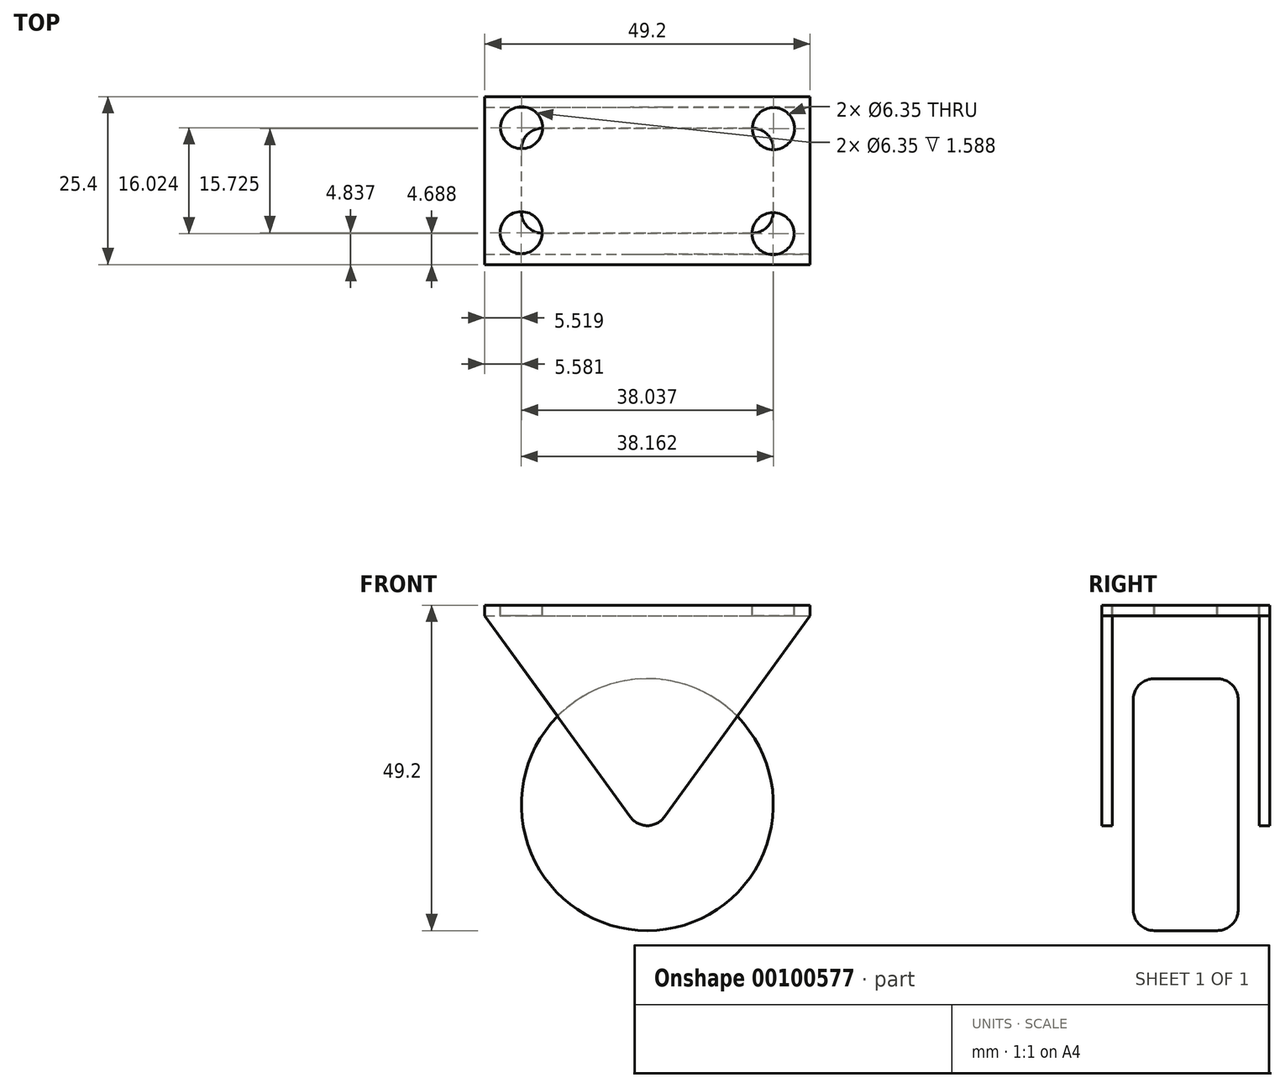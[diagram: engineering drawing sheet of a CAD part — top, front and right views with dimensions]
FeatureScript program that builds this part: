
annotation { "Feature Type Name" : "Feature", "Feature Type Description" : "" }
export const myFeature = defineFeature(function(context is Context, id is Id, definition is map)
    precondition{}
    {
        {
            var Q0;
            Q0=qCreatedBy(makeId("Front.planeOp"),FACE);
            var sketch = newSketch(context, id + "F0", { "sketchPlane" : qUnion([Q0])});
            skCircle(sketch, "E0", {"center": v(0, 0) * mm, "radius": 19.05 * mm});
            skSolve(sketch);
        }
        {
            var Q0;
            Q0=makeQuery(id+"F0.imprint","IMPRINT",FACE,{"disambiguationData":[TD([[makeQuery(id+"F0.imprint","IMPRINT",EDGE,{"derivedFrom":sQuery(id+"F0.wireOp",EDGE,"E0")}),1.0]])]});
            extrude(context, id + "F1", {"entities" : qUnion([Q0]), "endBound" : BoundingType.SYMMETRIC, "depth" : 15.88 * mm});
        }
        {
            var Q0;
            Q0=makeQuery(id+"F1.opExtrude","CAP_EDGE",EDGE,{"disambiguationData":[OSD([sQuery(id+"F0.wireOp",EDGE,"E0")])],"isStart":true});
            var Q1;
            Q1=makeQuery(id+"F1.opExtrude","CAP_EDGE",EDGE,{"disambiguationData":[OSD([sQuery(id+"F0.wireOp",EDGE,"E0")])],"isStart":false});
            fillet(context, id + "F2", {"entities" : qUnion([Q0, Q1]), "radius" : 3.17 * mm, "tangentPropagation" : true, "allowEdgeOverflow" : false});
        }
        {
            var Q0;
            Q0=qCreatedBy(makeId("Top.planeOp"),FACE);
            cPlane(context, id + "F3", {"entities" : qUnion([Q0]), "cplaneType" : CPlaneType.OFFSET, "offset" : 30.15 * mm, "width" : 152.4 * mm, "height" : 152.4 * mm});
        }
        {
            var Q0;
            Q0=qCreatedBy(id+"F3.planeOp",FACE);
            var sketch = newSketch(context, id + "F4", { "sketchPlane" : qUnion([Q0])});
            skLineSegment(sketch, "E1.bottom", {"start": v(-24.6, 12.7) * mm, "end": v(24.6, 12.7) * mm});
            skLineSegment(sketch, "E1.top", {"start": v(-24.6, -12.7) * mm, "end": v(24.6, -12.7) * mm});
            skLineSegment(sketch, "E1.left", {"start": v(-24.6, 12.7) * mm, "end": v(-24.6, -12.7) * mm});
            skLineSegment(sketch, "E1.right", {"start": v(24.6, 12.7) * mm, "end": v(24.6, -12.7) * mm});
            skCircle(sketch, "E2", {"center": v(-19.08, -7.86) * mm, "radius": 3.18 * mm});
            skCircle(sketch, "E3", {"center": v(-19.02, 8.01) * mm, "radius": 3.18 * mm});
            skCircle(sketch, "E4", {"center": v(19.08, 7.86) * mm, "radius": 3.18 * mm});
            skCircle(sketch, "E5", {"center": v(19.02, -8.01) * mm, "radius": 3.18 * mm});
            skLineSegment(sketch, "E6", {"start": v(-19.08, -7.86) * mm, "end": v(-19.02, 8.01) * mm, "construction": true});
            skLineSegment(sketch, "E7", {"start": v(19.08, 7.86) * mm, "end": v(-19.02, 8.01) * mm, "construction": true});
            skLineSegment(sketch, "E8", {"start": v(19.02, -8.01) * mm, "end": v(19.08, 7.86) * mm, "construction": true});
            skLineSegment(sketch, "E9", {"start": v(19.02, -8.01) * mm, "end": v(-19.08, -7.86) * mm, "construction": true});
            skSolve(sketch);
        }
        {
            var Q0;
            Q0=makeQuery(id+"F4.imprint","IMPRINT",FACE,{"disambiguationData":[TD([[makeQuery(id+"F4.imprint","IMPRINT",EDGE,{"derivedFrom":sQuery(id+"F4.wireOp",EDGE,"E1.bottom")}),-1.0]])]});
            extrude(context, id + "F5", {"entities" : qUnion([Q0]), "oppositeDirection" : true, "depth" : 1.59 * mm});
        }
        {
            var Q0;
            Q0=makeQuery(id+"F5.opExtrude","SWEPT_FACE",FACE,{"disambiguationData":[OSD([sQuery(id+"F4.wireOp",EDGE,"E1.top")])]});
            var sketch = newSketch(context, id + "F6", { "sketchPlane" : qUnion([Q0])});
            skArc(sketch, "E10", {"start": v(-2.57, -1.86) * mm, "mid": v(0, -3.18) * mm, "end": v(2.57, -1.86) * mm});
            skLineSegment(sketch, "E11", {"start": v(-24.6, 28.56) * mm, "end": v(-2.57, -1.86) * mm});
            skLineSegment(sketch, "E12", {"start": v(24.6, 28.56) * mm, "end": v(2.57, -1.86) * mm});
            skSolve(sketch);
        }
        {
            var Q0;
            Q0=makeQuery(id+"F6.imprint","IMPRINT",FACE,{"disambiguationData":[TD([[makeQuery(id+"F6.imprint","IMPRINT",EDGE,{"derivedFrom":sQuery(id+"F6.wireOp",EDGE,"E10")}),1.0]])]});
            extrude(context, id + "F7", {"entities" : qUnion([Q0]), "operationType" : NewBodyOperationType.ADD, "oppositeDirection" : true, "depth" : 1.59 * mm});
        }
        {
            var Q0;
            Q0=makeQuery(id+"F5.opExtrude","SWEPT_FACE",FACE,{"disambiguationData":[OSD([sQuery(id+"F4.wireOp",EDGE,"E1.bottom")])]});
            var sketch = newSketch(context, id + "F8", { "sketchPlane" : qUnion([Q0])});
            skArc(sketch, "E13", {"start": v(-2.57, -1.86) * mm, "mid": v(0, -3.18) * mm, "end": v(2.57, -1.86) * mm});
            skLineSegment(sketch, "E14", {"start": v(-24.6, 28.56) * mm, "end": v(-2.57, -1.86) * mm});
            skLineSegment(sketch, "E15", {"start": v(24.6, 28.56) * mm, "end": v(2.57, -1.86) * mm});
            skSolve(sketch);
        }
        {
            var Q0;
            Q0=makeQuery(id+"F8.imprint","IMPRINT",FACE,{"disambiguationData":[TD([[makeQuery(id+"F8.imprint","IMPRINT",EDGE,{"derivedFrom":sQuery(id+"F8.wireOp",EDGE,"E13")}),1.0]])]});
            extrude(context, id + "F9", {"entities" : qUnion([Q0]), "operationType" : NewBodyOperationType.ADD, "oppositeDirection" : true, "depth" : 1.59 * mm});
        }
    });
